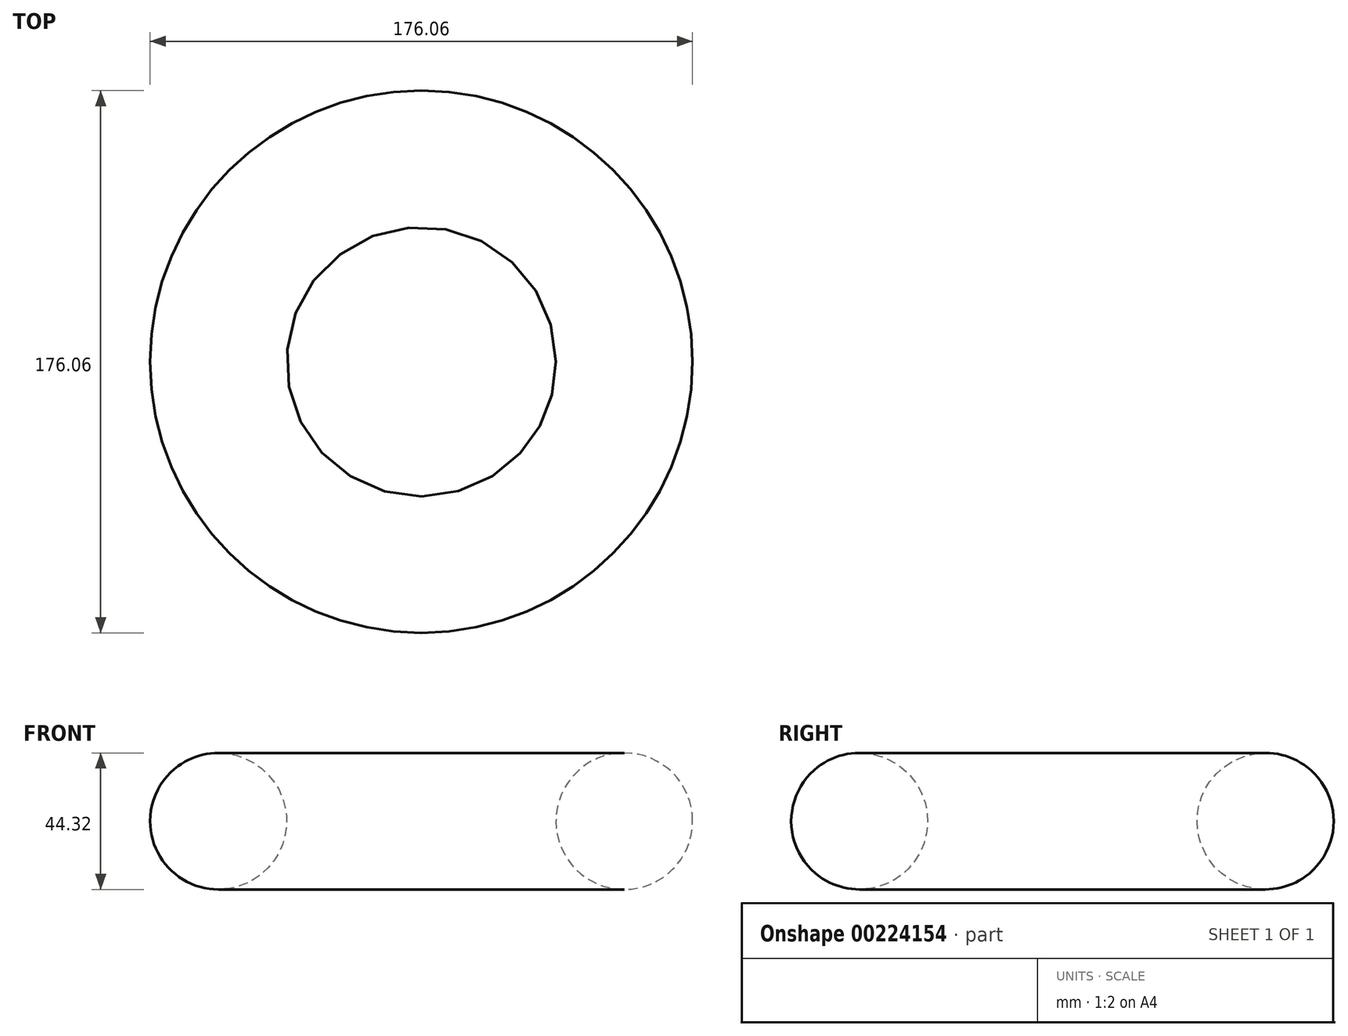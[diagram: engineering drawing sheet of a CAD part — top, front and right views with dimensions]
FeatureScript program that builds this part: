
annotation { "Feature Type Name" : "Feature", "Feature Type Description" : "" }
export const myFeature = defineFeature(function(context is Context, id is Id, definition is map)
    precondition{}
    {
        {
            var Q0;
            Q0=qCreatedBy(makeId("Front.planeOp"),FACE);
            var sketch = newSketch(context, id + "F0", { "sketchPlane" : qUnion([Q0])});
            skCircle(sketch, "E0", {"center": v(0, 0) * mm, "radius": 22.16 * mm});
            skSolve(sketch);
        }
        {
            var Q0;
            Q0=qCreatedBy(makeId("Front.planeOp"),FACE);
            var sketch = newSketch(context, id + "F1", { "sketchPlane" : qUnion([Q0])});
            skLineSegment(sketch, "E1", {"start": v(-65.87, 23.76) * mm, "end": v(-65.87, -29.3) * mm});
            skSolve(sketch);
        }
        {
            var Q0;
            Q0=makeQuery(id+"F0.imprint","IMPRINT",FACE,{"disambiguationData":[TD([[makeQuery(id+"F0.imprint","IMPRINT",EDGE,{"derivedFrom":sQuery(id+"F0.wireOp",EDGE,"E0")}),1.0]])]});
            var Q1;
            Q1=sQuery(id+"F1.wireOp",EDGE,"E1");
            revolve(context, id + "F2", {"entities" : qUnion([Q0]), "axis" : qUnion([Q1]), "revolveType" : RevolveType.FULL});
        }
    });
